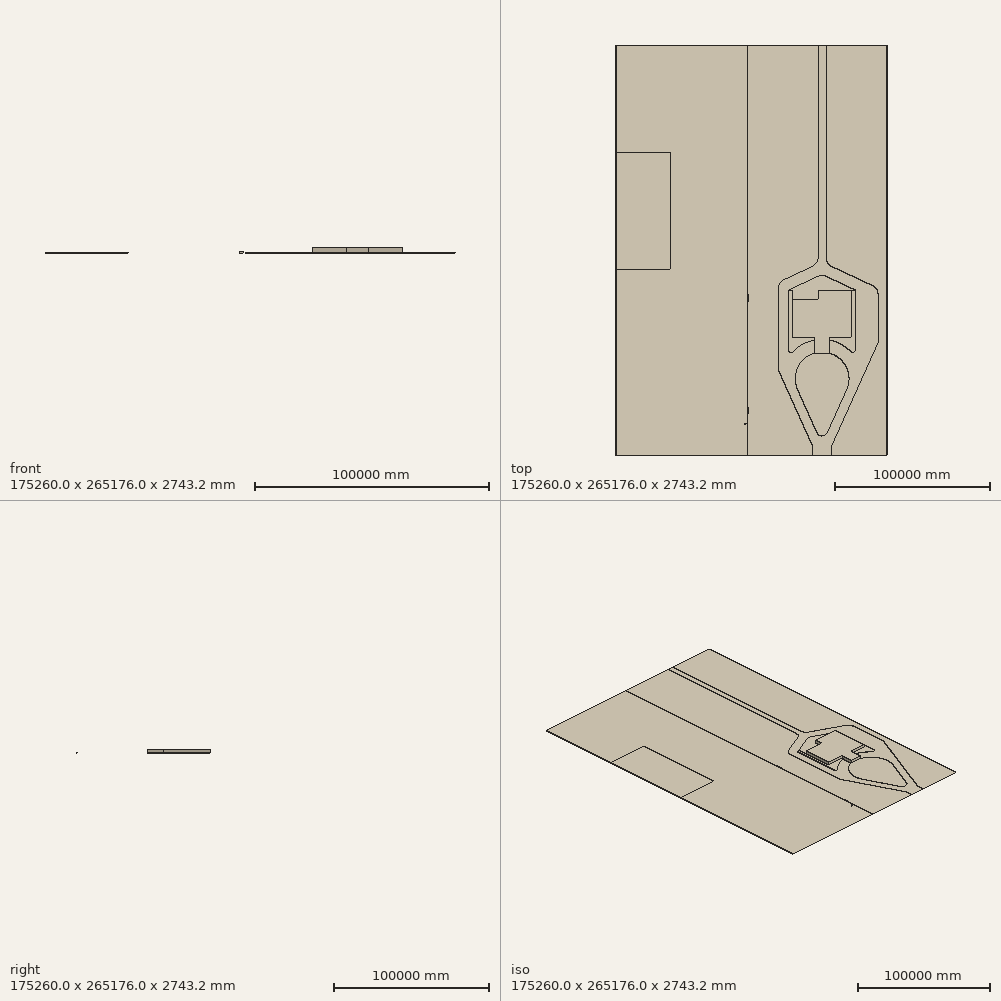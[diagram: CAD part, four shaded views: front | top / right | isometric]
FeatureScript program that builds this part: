
annotation { "Feature Type Name" : "Feature", "Feature Type Description" : "" }
export const myFeature = defineFeature(function(context is Context, id is Id, definition is map)
    precondition{}
    {
        {
            var Q0;
            Q0=qCreatedBy(makeId("Top.planeOp"),FACE);
            var sketch = newSketch(context, id + "F0", { "sketchPlane" : qUnion([Q0])});
            skLineSegment(sketch, "E0.bottom", {"start": v(-85344, 0) * mm, "end": v(89916, 0) * mm});
            skLineSegment(sketch, "E0.top", {"start": v(-85344, 265176) * mm, "end": v(89916, 265176) * mm});
            skLineSegment(sketch, "E0.left", {"start": v(-85344, 0) * mm, "end": v(-85344, 265176) * mm});
            skLineSegment(sketch, "E0.right", {"start": v(89916, 0) * mm, "end": v(89916, 265176) * mm});
            skSolve(sketch);
        }
        {
            var Q0;
            Q0 = qSketchRegion(id + "F0", true);
            extrude(context, id + "F1", {"entities" : qUnion([Q0]), "depth" : 304.8 * mm, "offsetDistance" : 30.48 * mm});
        }
        {
            var Q0;
            Q0=makeQuery(id+"F1.opExtrude","CAP_FACE",FACE,{"disambiguationData":[OSD([sQuery(id+"F0.wireOp",EDGE,"E0.bottom"),sQuery(id+"F0.wireOp",EDGE,"E0.top"),sQuery(id+"F0.wireOp",EDGE,"E0.left"),sQuery(id+"F0.wireOp",EDGE,"E0.right")])],"isStart":false});
            var sketch = newSketch(context, id + "F2", { "sketchPlane" : qUnion([Q0])});
            skLineSegment(sketch, "E1.bottom", {"start": v(0, 0) * mm, "end": v(-85344, 0) * mm});
            skLineSegment(sketch, "E1.top", {"start": v(0, 265176) * mm, "end": v(-85344, 265176) * mm});
            skLineSegment(sketch, "E1.left", {"start": v(0, 0) * mm, "end": v(0, 265176) * mm});
            skLineSegment(sketch, "E1.right", {"start": v(-85344, 0) * mm, "end": v(-85344, 265176) * mm});
            skSolve(sketch);
        }
        {
            var Q0;
            Q0 = qSketchRegion(id + "F2", true);
            extrude(context, id + "F3", {"entities" : qUnion([Q0]), "operationType" : NewBodyOperationType.REMOVE, "oppositeDirection" : true, "depth" : 30.48 * mm, "offsetDistance" : 30.48 * mm});
        }
        {
            var Q0;
            Q0=makeQuery(id+"F3.boolean.opBoolean","COPY",FACE,{"derivedFrom":makeQuery(id+"F3.opExtrude","CAP_FACE",FACE,{"disambiguationData":[OSD([sQuery(id+"F2.wireOp",EDGE,"E1.bottom"),sQuery(id+"F2.wireOp",EDGE,"E1.top"),sQuery(id+"F2.wireOp",EDGE,"E1.left"),sQuery(id+"F2.wireOp",EDGE,"E1.right")])],"isStart":false})});
            var sketch = newSketch(context, id + "F4", { "sketchPlane" : qUnion([Q0])});
            skLineSegment(sketch, "E2.bottom", {"start": v(-85344, 120396) * mm, "end": v(-49987.2, 120396) * mm});
            skLineSegment(sketch, "E2.top", {"start": v(-85344, 195986.4) * mm, "end": v(-49987.2, 195986.4) * mm});
            skLineSegment(sketch, "E2.left", {"start": v(-85344, 120396) * mm, "end": v(-85344, 195986.4) * mm});
            skLineSegment(sketch, "E2.right", {"start": v(-49987.2, 120396) * mm, "end": v(-49987.2, 195986.4) * mm});
            skSolve(sketch);
        }
        {
            var Q0;
            Q0 = qSketchRegion(id + "F4", true);
            extrude(context, id + "F5", {"entities" : qUnion([Q0]), "operationType" : NewBodyOperationType.ADD, "depth" : 30.48 * mm, "offsetDistance" : 30.48 * mm});
        }
        {
            var Q0;
            Q0=makeQuery(id+"F1.opExtrude","CAP_FACE",FACE,{"disambiguationData":[OSD([sQuery(id+"F0.wireOp",EDGE,"E0.bottom"),sQuery(id+"F0.wireOp",EDGE,"E0.top"),sQuery(id+"F0.wireOp",EDGE,"E0.left"),sQuery(id+"F0.wireOp",EDGE,"E0.right")])],"isStart":false});
            var sketch = newSketch(context, id + "F6", { "sketchPlane" : qUnion([Q0])});
            skLineSegment(sketch, "E3.bottom", {"start": v(-152.4, 104241.6) * mm, "end": v(152.4, 104241.6) * mm});
            skLineSegment(sketch, "E3.top", {"start": v(-152.4, 98755.2) * mm, "end": v(152.4, 98755.2) * mm});
            skLineSegment(sketch, "E3.left", {"start": v(-152.4, 104241.6) * mm, "end": v(-152.4, 98755.2) * mm});
            skLineSegment(sketch, "E3.right", {"start": v(152.4, 104241.6) * mm, "end": v(152.4, 98755.2) * mm});
            skLineSegment(sketch, "E4.bottom", {"start": v(-152.4, 26517.6) * mm, "end": v(152.4, 26517.6) * mm});
            skLineSegment(sketch, "E4.top", {"start": v(-152.4, 31089.6) * mm, "end": v(152.4, 31089.6) * mm});
            skLineSegment(sketch, "E4.left", {"start": v(-152.4, 26517.6) * mm, "end": v(-152.4, 31089.6) * mm});
            skLineSegment(sketch, "E4.right", {"start": v(152.4, 26517.6) * mm, "end": v(152.4, 31089.6) * mm});
            skSolve(sketch);
        }
        {
            var Q0;
            Q0 = qSketchRegion(id + "F6", true);
            extrude(context, id + "F7", {"entities" : qUnion([Q0]), "operationType" : NewBodyOperationType.ADD, "depth" : 60.96 * mm, "offsetDistance" : 30.48 * mm});
        }
        {
            var Q0;
            Q0=makeQuery(id+"F1.opExtrude","CAP_FACE",FACE,{"disambiguationData":[OSD([sQuery(id+"F0.wireOp",EDGE,"E0.bottom"),sQuery(id+"F0.wireOp",EDGE,"E0.top"),sQuery(id+"F0.wireOp",EDGE,"E0.left"),sQuery(id+"F0.wireOp",EDGE,"E0.right")])],"isStart":false});
            var sketch = newSketch(context, id + "F8", { "sketchPlane" : qUnion([Q0])});
            skLineSegment(sketch, "E5", {"start": v(28956, 100584) * mm, "end": v(28956, 76200) * mm});
            skLineSegment(sketch, "E6", {"start": v(28956, 76200) * mm, "end": v(43129.2, 76200) * mm});
            skLineSegment(sketch, "E7", {"start": v(67056, 76200) * mm, "end": v(67056, 106984.8) * mm});
            skLineSegment(sketch, "E8", {"start": v(67056, 106984.8) * mm, "end": v(45720, 106984.8) * mm});
            skLineSegment(sketch, "E9", {"start": v(45720, 106984.8) * mm, "end": v(45720, 100584) * mm});
            skLineSegment(sketch, "E10", {"start": v(45720, 100584) * mm, "end": v(28956, 100584) * mm});
            skLineSegment(sketch, "E11", {"start": v(43129.2, 76200) * mm, "end": v(43129.2, 66141.6) * mm});
            skLineSegment(sketch, "E12", {"start": v(43129.2, 66141.6) * mm, "end": v(52882.8, 66141.6) * mm});
            skLineSegment(sketch, "E13", {"start": v(52882.8, 66141.6) * mm, "end": v(52882.8, 76200) * mm});
            skLineSegment(sketch, "E14.trimOffspring", {"start": v(52882.8, 76200) * mm, "end": v(67056, 76200) * mm});
            skSolve(sketch);
        }
        {
            var Q0;
            Q0 = qSketchRegion(id + "F8", true);
            extrude(context, id + "F9", {"entities" : qUnion([Q0]), "operationType" : NewBodyOperationType.ADD, "depth" : 2438.4 * mm, "offsetDistance" : 30.48 * mm});
        }
        {
            var Q0;
            Q0=makeQuery(id+"F1.opExtrude","CAP_FACE",FACE,{"disambiguationData":[OSD([sQuery(id+"F0.wireOp",EDGE,"E0.bottom"),sQuery(id+"F0.wireOp",EDGE,"E0.top"),sQuery(id+"F0.wireOp",EDGE,"E0.left"),sQuery(id+"F0.wireOp",EDGE,"E0.right")])],"isStart":false});
            var sketch = newSketch(context, id + "F10", { "sketchPlane" : qUnion([Q0])});
            skArc(sketch, "E15", {"start": v(44531.2, 14833.08) * mm, "mid": v(48006, 12585.7) * mm, "end": v(51480.8, 14833.08) * mm});
            skArc(sketch, "E16", {"start": v(63851.13, 42340.93) * mm, "mid": v(48006, 66840.1) * mm, "end": v(32160.87, 42340.93) * mm});
            skLineSegment(sketch, "E17", {"start": v(44531.2, 14833.08) * mm, "end": v(32160.87, 42340.93) * mm});
            skLineSegment(sketch, "E18", {"start": v(63851.13, 42340.93) * mm, "end": v(51480.8, 14833.08) * mm});
            skLineSegment(sketch, "E19", {"start": v(48006, 49466.5) * mm, "end": v(48006, 16395.7) * mm, "construction": true});
            skLineSegment(sketch, "E20", {"start": v(41757.6, 0) * mm, "end": v(41757.6, 6137.42) * mm});
            skLineSegment(sketch, "E21", {"start": v(41757.6, 6137.42) * mm, "end": v(22404.48, 49172.9) * mm});
            skLineSegment(sketch, "E22", {"start": v(54254.4, 0) * mm, "end": v(54254.4, 6137.42) * mm});
            skLineSegment(sketch, "E23", {"start": v(54254.4, 6137.42) * mm, "end": v(73607.52, 49172.9) * mm});
            skArc(sketch, "E24", {"start": v(73607.52, 49172.9) * mm, "mid": v(48006, 75069.7) * mm, "end": v(22404.48, 49172.9) * mm});
            skLineSegment(sketch, "E25", {"start": v(41757.6, 0) * mm, "end": v(54254.4, 0) * mm});
            skLineSegment(sketch, "E26", {"start": v(48006, 0) * mm, "end": v(48006, 16395.7) * mm, "construction": true});
            skSolve(sketch);
        }
        {
            var Q0;
            Q0 = qSketchRegion(id + "F10", true);
            extrude(context, id + "F11", {"entities" : qUnion([Q0]), "operationType" : NewBodyOperationType.REMOVE, "oppositeDirection" : true, "depth" : 30.48 * mm, "offsetDistance" : 30.48 * mm});
        }
        {
            var Q0;
            {var subQ5=sQuery(id+"F0.wireOp",EDGE,"E0.top");var subQ6=sQuery(id+"F0.wireOp",EDGE,"E0.right");var subQ10=sQuery(id+"F0.wireOp",EDGE,"E0.bottom");Q0=makeQuery(id+"F11.boolean.opBoolean","SPLIT",FACE,{"disambiguationData":[TD([makeQuery(id+"F1.opExtrude","SWEPT_FACE",FACE,{"disambiguationData":[OSD([subQ10])]})])],"derivedFrom":makeQuery(id+"F1.opExtrude","CAP_FACE",FACE,{"disambiguationData":[OSD([subQ10,subQ5,sQuery(id+"F0.wireOp",EDGE,"E0.left"),subQ6])],"isStart":false})});}
            var sketch = newSketch(context, id + "F12", { "sketchPlane" : qUnion([Q0])});
            skLineSegment(sketch, "E27", {"start": v(28956, 100584) * mm, "end": v(28956, 106984.8) * mm});
            skLineSegment(sketch, "E28", {"start": v(28956, 106984.8) * mm, "end": v(26517.6, 106984.8) * mm});
            skLineSegment(sketch, "E29", {"start": v(26517.6, 106984.8) * mm, "end": v(26517.6, 67832.44) * mm});
            skLineSegment(sketch, "E30", {"start": v(67056, 106984.8) * mm, "end": v(69494.4, 106984.8) * mm});
            skLineSegment(sketch, "E31", {"start": v(69494.4, 106984.8) * mm, "end": v(69494.4, 67832.44) * mm});
            skArc(sketch, "E32.0", {"start": v(43129.2, 74600.96) * mm, "mid": v(35521.37, 71819.53) * mm, "end": v(29163.2, 66800.65) * mm});
            skArc(sketch, "E33.0", {"start": v(66848.8, 66800.65) * mm, "mid": v(60490.63, 71819.53) * mm, "end": v(52882.8, 74600.96) * mm});
            skLineSegment(sketch, "E34.0", {"start": v(28956, 100584) * mm, "end": v(28956, 76200) * mm});
            skLineSegment(sketch, "E35.0", {"start": v(28956, 76200) * mm, "end": v(43129.2, 76200) * mm});
            skLineSegment(sketch, "E36.0", {"start": v(43129.2, 76200) * mm, "end": v(43129.2, 74600.96) * mm});
            skLineSegment(sketch, "E37.0", {"start": v(52882.8, 74600.96) * mm, "end": v(52882.8, 76200) * mm});
            skLineSegment(sketch, "E38.0", {"start": v(52882.8, 76200) * mm, "end": v(67056, 76200) * mm});
            skLineSegment(sketch, "E39.0", {"start": v(67056, 76200) * mm, "end": v(67056, 106984.8) * mm});
            skArc(sketch, "E40", {"start": v(26517.6, 67832.44) * mm, "mid": v(27487.86, 66412.6) * mm, "end": v(29163.2, 66800.65) * mm});
            skArc(sketch, "E41", {"start": v(66848.8, 66800.65) * mm, "mid": v(68524.14, 66412.6) * mm, "end": v(69494.4, 67832.44) * mm});
            skPoint(sketch, "E42.orphan", {"position": v(73607.52, 49172.9) * mm});
            skPoint(sketch, "E43.orphan", {"position": v(22404.48, 49172.9) * mm});
            skSolve(sketch);
        }
        {
            var Q0;
            Q0 = qSketchRegion(id + "F12", true);
            extrude(context, id + "F13", {"entities" : qUnion([Q0]), "operationType" : NewBodyOperationType.ADD, "depth" : 152.4 * mm, "offsetDistance" : 30.48 * mm});
        }
        {
            var Q0;
            {var subQ5=sQuery(id+"F0.wireOp",EDGE,"E0.top");var subQ6=sQuery(id+"F0.wireOp",EDGE,"E0.right");var subQ10=sQuery(id+"F0.wireOp",EDGE,"E0.bottom");Q0=makeQuery(id+"F11.boolean.opBoolean","SPLIT",FACE,{"disambiguationData":[TD([makeQuery(id+"F1.opExtrude","SWEPT_FACE",FACE,{"disambiguationData":[OSD([subQ10])]})])],"derivedFrom":makeQuery(id+"F1.opExtrude","CAP_FACE",FACE,{"disambiguationData":[OSD([subQ10,subQ5,sQuery(id+"F0.wireOp",EDGE,"E0.left"),subQ6])],"isStart":false})});}
            var sketch = newSketch(context, id + "F14", { "sketchPlane" : qUnion([Q0])});
            skLineSegment(sketch, "E44", {"start": v(19812, 108045.55) * mm, "end": v(19812, 54937.8) * mm});
            skLineSegment(sketch, "E45", {"start": v(19812, 54937.8) * mm, "end": v(22404.48, 49172.9) * mm});
            skLineSegment(sketch, "E46", {"start": v(73607.52, 49172.9) * mm, "end": v(84124.8, 72560.16) * mm});
            skLineSegment(sketch, "E47", {"start": v(84124.8, 72560.16) * mm, "end": v(84124.8, 104331.13) * mm});
            skLineSegment(sketch, "E48", {"start": v(26517.6, 106984.8) * mm, "end": v(46712.42, 116450.28) * mm});
            skLineSegment(sketch, "E49", {"start": v(49299.58, 116450.28) * mm, "end": v(69494.4, 106984.8) * mm});
            skLineSegment(sketch, "E50", {"start": v(45415.2, 265176) * mm, "end": v(45415.2, 127796.28) * mm});
            skLineSegment(sketch, "E51", {"start": v(50596.8, 265176) * mm, "end": v(50596.8, 127796.28) * mm});
            skLineSegment(sketch, "E52", {"start": v(54105.64, 122276.51) * mm, "end": v(80615.96, 109850.9) * mm});
            skLineSegment(sketch, "E53", {"start": v(41906.36, 122276.51) * mm, "end": v(23320.84, 113565.32) * mm});
            skPoint(sketch, "E54.visualSharp", {"position": v(48006, 117056.6) * mm});
            skArc(sketch, "E54.filletArc", {"start": v(49299.58, 116450.28) * mm, "mid": v(48006, 116738.4) * mm, "end": v(46712.42, 116450.28) * mm});
            skLineSegment(sketch, "E55", {"start": v(45415.2, 123921.13) * mm, "end": v(50596.8, 123921.13) * mm, "construction": true});
            skLineSegment(sketch, "E56", {"start": v(48006, 123921.13) * mm, "end": v(48006, 66141.6) * mm, "construction": true});
            skLineSegment(sketch, "E57", {"start": v(45415.2, 265176) * mm, "end": v(50596.8, 265176) * mm});
            skPoint(sketch, "E58.visualSharp", {"position": v(19812, 111920.7) * mm});
            skArc(sketch, "E58.filletArc", {"start": v(23320.84, 113565.32) * mm, "mid": v(20763.46, 111315.87) * mm, "end": v(19812, 108045.55) * mm});
            skPoint(sketch, "E59.visualSharp", {"position": v(84124.8, 108206.28) * mm});
            skArc(sketch, "E59.filletArc", {"start": v(84124.8, 104331.13) * mm, "mid": v(83173.34, 107601.44) * mm, "end": v(80615.96, 109850.9) * mm});
            skPoint(sketch, "E60.visualSharp", {"position": v(45415.2, 123921.13) * mm});
            skArc(sketch, "E60.filletArc", {"start": v(41906.36, 122276.51) * mm, "mid": v(44463.74, 124525.96) * mm, "end": v(45415.2, 127796.28) * mm});
            skPoint(sketch, "E61.visualSharp", {"position": v(50596.8, 123921.13) * mm});
            skArc(sketch, "E61.filletArc", {"start": v(50596.8, 127796.28) * mm, "mid": v(51548.26, 124525.96) * mm, "end": v(54105.64, 122276.51) * mm});
            skArc(sketch, "E62.0", {"start": v(29163.2, 66800.65) * mm, "mid": v(24099.75, 58632.48) * mm, "end": v(22404.48, 49172.9) * mm});
            skArc(sketch, "E63.0", {"start": v(26517.6, 67832.44) * mm, "mid": v(27487.86, 66412.6) * mm, "end": v(29163.2, 66800.65) * mm});
            skLineSegment(sketch, "E64.0", {"start": v(26517.6, 106984.8) * mm, "end": v(26517.6, 67832.44) * mm});
            skLineSegment(sketch, "E65.0", {"start": v(69494.4, 106984.8) * mm, "end": v(69494.4, 67832.44) * mm});
            skArc(sketch, "E66.0", {"start": v(66848.8, 66800.65) * mm, "mid": v(68524.14, 66412.6) * mm, "end": v(69494.4, 67832.44) * mm});
            skArc(sketch, "E67.0", {"start": v(73607.52, 49172.9) * mm, "mid": v(71912.25, 58632.48) * mm, "end": v(66848.8, 66800.65) * mm});
            skSolve(sketch);
        }
        {
            var Q0;
            Q0 = qSketchRegion(id + "F14", true);
            extrude(context, id + "F15", {"entities" : qUnion([Q0]), "operationType" : NewBodyOperationType.REMOVE, "oppositeDirection" : true, "depth" : 30.48 * mm, "offsetDistance" : 30.48 * mm});
        }
        {
            var Q0;
            Q0=makeQuery(id+"F3.boolean.opBoolean","COPY",FACE,{"derivedFrom":makeQuery(id+"F3.opExtrude","CAP_FACE",FACE,{"disambiguationData":[OSD([sQuery(id+"F2.wireOp",EDGE,"E1.bottom"),sQuery(id+"F2.wireOp",EDGE,"E1.top"),sQuery(id+"F2.wireOp",EDGE,"E1.left"),sQuery(id+"F2.wireOp",EDGE,"E1.right")])],"isStart":false})});
            var sketch = newSketch(context, id + "F16", { "sketchPlane" : qUnion([Q0])});
            skLineSegment(sketch, "E68.bottom", {"start": v(-2438.4, 20726.4) * mm, "end": v(-914.4, 20726.4) * mm});
            skLineSegment(sketch, "E68.top", {"start": v(-2438.4, 19812) * mm, "end": v(-914.4, 19812) * mm});
            skLineSegment(sketch, "E68.left", {"start": v(-2438.4, 20726.4) * mm, "end": v(-2438.4, 19812) * mm});
            skLineSegment(sketch, "E68.right", {"start": v(-914.4, 20726.4) * mm, "end": v(-914.4, 19812) * mm});
            skSolve(sketch);
        }
        {
            var Q0;
            Q0=makeQuery(id+"F16.imprint","IMPRINT",FACE,{"disambiguationData":[TD([[makeQuery(id+"F16.imprint","IMPRINT",EDGE,{"derivedFrom":sQuery(id+"F16.wireOp",EDGE,"E68.bottom")}),-1.0]])]});
            extrude(context, id + "F17", {"entities" : qUnion([Q0]), "operationType" : NewBodyOperationType.ADD, "depth" : 609.6 * mm, "offsetDistance" : 30.48 * mm});
        }
    });
